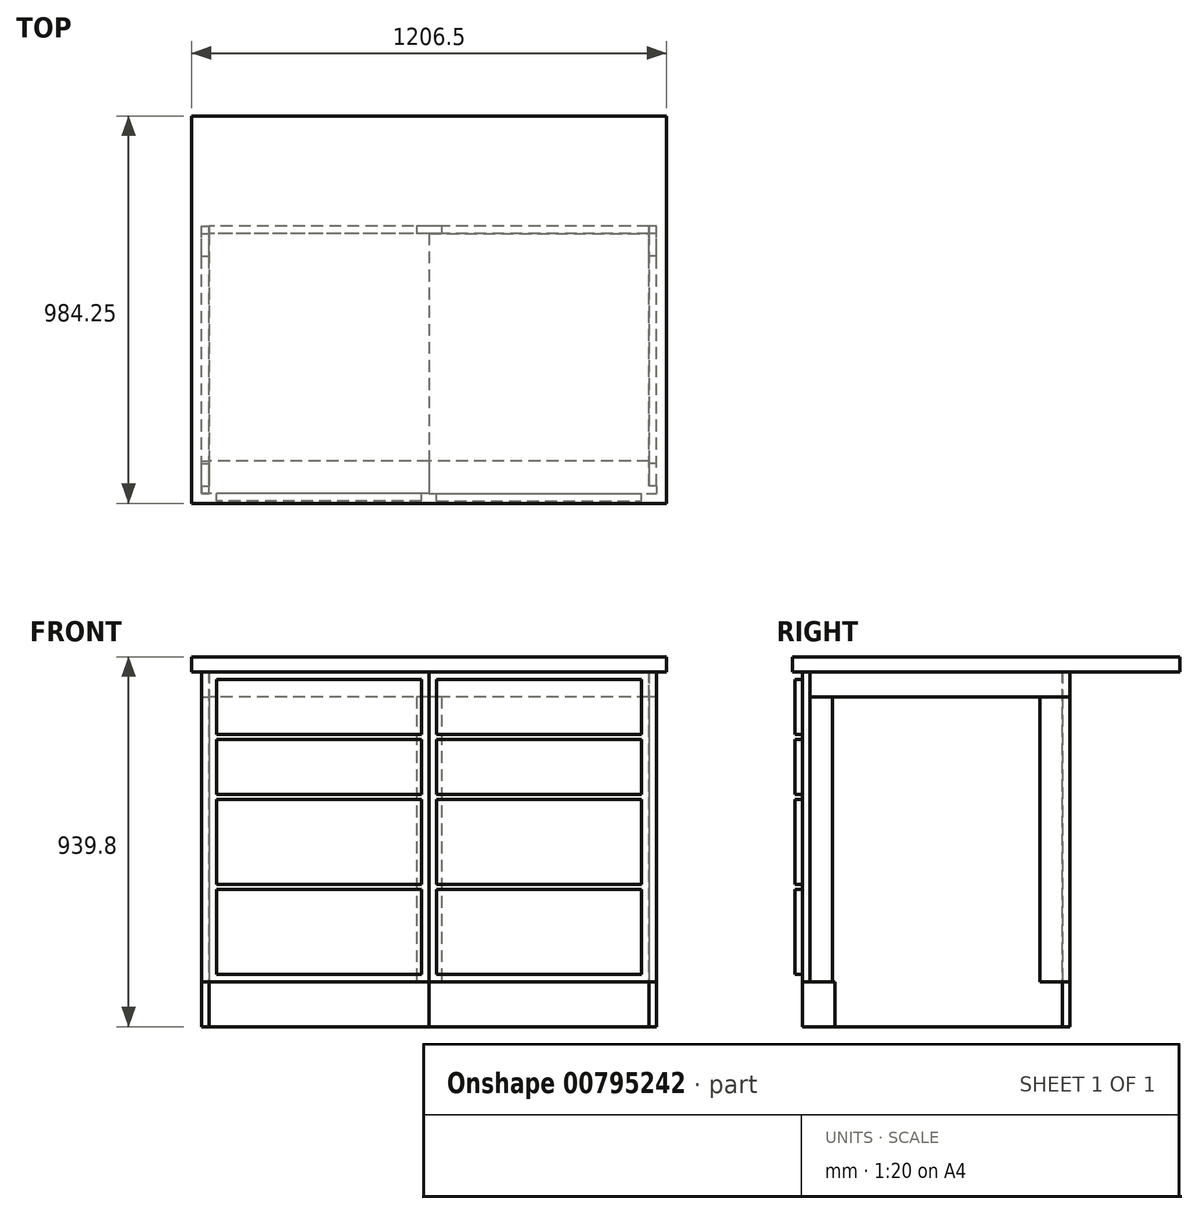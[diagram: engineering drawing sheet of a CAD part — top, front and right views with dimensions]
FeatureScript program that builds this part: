
annotation { "Feature Type Name" : "Feature", "Feature Type Description" : "" }
export const myFeature = defineFeature(function(context is Context, id is Id, definition is map)
    precondition{}
    {
        {
            var Q0;
            Q0=qCreatedBy(makeId("Top.planeOp"),FACE);
            var sketch = newSketch(context, id + "F0", { "sketchPlane" : qUnion([Q0])});
            skLineSegment(sketch, "E0.bottom", {"start": v(0, 328.85) * mm, "end": v(-558.8, 328.85) * mm});
            skLineSegment(sketch, "E0.top", {"start": v(0, -331.55) * mm, "end": v(-558.8, -331.55) * mm});
            skLineSegment(sketch, "E0.left", {"start": v(0, 328.85) * mm, "end": v(0, -331.55) * mm});
            skLineSegment(sketch, "E0.right", {"start": v(-558.8, 328.85) * mm, "end": v(-558.8, -331.55) * mm});
            skLineSegment(sketch, "E1.bottom", {"start": v(0, 328.85) * mm, "end": v(558.8, 328.85) * mm});
            skLineSegment(sketch, "E1.top", {"start": v(0, -331.55) * mm, "end": v(558.8, -331.55) * mm});
            skLineSegment(sketch, "E1.right", {"start": v(558.8, 328.85) * mm, "end": v(558.8, -331.55) * mm});
            skSolve(sketch);
        }
        {
            var Q0;
            Q0=makeQuery(id+"F0.imprint","IMPRINT",FACE,{"disambiguationData":[TD([[makeQuery(id+"F0.imprint","IMPRINT",EDGE,{"derivedFrom":sQuery(id+"F0.wireOp",EDGE,"E0.bottom")}),1.0]])]});
            extrude(context, id + "F1", {"entities" : qUnion([Q0]), "oppositeDirection" : true, "depth" : 901.7 * mm, "offsetDistance" : 25.4 * mm});
        }
        {
            var Q0;
            Q0=makeQuery(id+"F0.imprint","IMPRINT",FACE,{"disambiguationData":[TD([[makeQuery(id+"F0.imprint","IMPRINT",EDGE,{"derivedFrom":sQuery(id+"F0.wireOp",EDGE,"E1.bottom")}),-1.0]])]});
            extrude(context, id + "F2", {"entities" : qUnion([Q0]), "oppositeDirection" : true, "depth" : 901.7 * mm, "offsetDistance" : 25.4 * mm});
        }
        {
            var Q0;
            Q0=makeQuery(id+"F1.opExtrude","SWEPT_FACE",FACE,{"disambiguationData":[OSD([sQuery(id+"F0.wireOp",EDGE,"E0.top")])]});
            var sketch = newSketch(context, id + "F3", { "sketchPlane" : qUnion([Q0])});
            skLineSegment(sketch, "E2.bottom", {"start": v(-558.8, -901.7) * mm, "end": v(558.8, -901.7) * mm});
            skLineSegment(sketch, "E2.top", {"start": v(-558.8, -787.4) * mm, "end": v(558.8, -787.4) * mm});
            skLineSegment(sketch, "E2.left", {"start": v(-558.8, -901.7) * mm, "end": v(-558.8, -787.4) * mm});
            skLineSegment(sketch, "E2.right", {"start": v(558.8, -901.7) * mm, "end": v(558.8, -787.4) * mm});
            skSolve(sketch);
        }
        {
            var Q0;
            {var subQ4=sQuery(id+"F3.wireOp",EDGE,"E2.left");Q0=makeQuery(id+"F3.imprint","IMPRINT",FACE,{"disambiguationData":[TD([[makeQuery(id+"F3.imprint","IMPRINT",EDGE,{"derivedFrom":subQ4}),-1.0]])]});}
            var Q1;
            {var subQ3=sQuery(id+"F3.wireOp",EDGE,"E2.right");Q1=makeQuery(id+"F3.imprint","IMPRINT",FACE,{"disambiguationData":[TD([[makeQuery(id+"F3.imprint","IMPRINT",EDGE,{"derivedFrom":subQ3}),1.0]])]});}
            extrude(context, id + "F4", {"entities" : qUnion([Q0, Q1]), "operationType" : NewBodyOperationType.REMOVE, "oppositeDirection" : true, "depth" : 82.55 * mm, "offsetDistance" : 25.4 * mm});
        }
        {
            var Q0;
            Q0=makeQuery(id+"F1.opExtrude","SWEPT_FACE",FACE,{"disambiguationData":[OSD([sQuery(id+"F0.wireOp",EDGE,"E0.right")])]});
            var sketch = newSketch(context, id + "F5", { "sketchPlane" : qUnion([Q0])});
            skLineSegment(sketch, "E3.bottom", {"start": v(331.55, 0) * mm, "end": v(312.5, 0) * mm});
            skLineSegment(sketch, "E3.top", {"start": v(331.55, -787.4) * mm, "end": v(312.5, -787.4) * mm});
            skLineSegment(sketch, "E3.left", {"start": v(331.55, 0) * mm, "end": v(331.55, -787.4) * mm});
            skLineSegment(sketch, "E3.right", {"start": v(312.5, 0) * mm, "end": v(312.5, -787.4) * mm});
            skSolve(sketch);
        }
        {
            var Q0;
            Q0=makeQuery(id+"F5.imprint","IMPRINT",FACE,{"disambiguationData":[TD([[makeQuery(id+"F5.imprint","IMPRINT",EDGE,{"derivedFrom":sQuery(id+"F5.wireOp",EDGE,"E3.bottom")}),-1.0]])]});
            extrude(context, id + "F6", {"entities" : qUnion([Q0]), "operationType" : NewBodyOperationType.ADD, "depth" : 19.05 * mm, "offsetDistance" : 25.4 * mm});
        }
        {
            var Q0;
            Q0=makeQuery(id+"F2.opExtrude","SWEPT_FACE",FACE,{"disambiguationData":[OSD([sQuery(id+"F0.wireOp",EDGE,"E1.right")])]});
            var sketch = newSketch(context, id + "F7", { "sketchPlane" : qUnion([Q0])});
            skLineSegment(sketch, "E4.bottom", {"start": v(-331.55, 0) * mm, "end": v(-312.5, 0) * mm});
            skLineSegment(sketch, "E4.top", {"start": v(-331.55, -787.4) * mm, "end": v(-312.5, -787.4) * mm});
            skLineSegment(sketch, "E4.left", {"start": v(-331.55, 0) * mm, "end": v(-331.55, -787.4) * mm});
            skLineSegment(sketch, "E4.right", {"start": v(-312.5, 0) * mm, "end": v(-312.5, -787.4) * mm});
            skSolve(sketch);
        }
        {
            var Q0;
            Q0=makeQuery(id+"F7.imprint","IMPRINT",FACE,{"disambiguationData":[TD([[makeQuery(id+"F7.imprint","IMPRINT",EDGE,{"derivedFrom":sQuery(id+"F7.wireOp",EDGE,"E4.bottom")}),1.0]])]});
            extrude(context, id + "F8", {"entities" : qUnion([Q0]), "operationType" : NewBodyOperationType.ADD, "depth" : 19.05 * mm, "offsetDistance" : 25.4 * mm});
        }
        {
            var Q0;
            Q0=makeQuery(id+"F1.opExtrude","SWEPT_FACE",FACE,{"disambiguationData":[OSD([sQuery(id+"F0.wireOp",EDGE,"E0.right")])]});
            var sketch = newSketch(context, id + "F9", { "sketchPlane" : qUnion([Q0])});
            skLineSegment(sketch, "E5.bottom", {"start": v(331.55, -901.7) * mm, "end": v(-347.9, -901.7) * mm});
            skLineSegment(sketch, "E5.top", {"start": v(331.55, -787.4) * mm, "end": v(-347.9, -787.4) * mm});
            skLineSegment(sketch, "E5.left", {"start": v(331.55, -901.7) * mm, "end": v(331.55, -787.4) * mm});
            skLineSegment(sketch, "E5.right", {"start": v(-347.9, -901.7) * mm, "end": v(-347.9, -787.4) * mm});
            skLineSegment(sketch, "E6.bottom", {"start": v(331.55, 0) * mm, "end": v(-347.9, 0) * mm});
            skLineSegment(sketch, "E6.top", {"start": v(331.55, -63.5) * mm, "end": v(-347.9, -63.5) * mm});
            skLineSegment(sketch, "E6.left", {"start": v(331.55, 0) * mm, "end": v(331.55, -63.5) * mm});
            skLineSegment(sketch, "E6.right", {"start": v(-347.9, 0) * mm, "end": v(-347.9, -63.5) * mm});
            skLineSegment(sketch, "E7.bottom", {"start": v(-347.9, -63.5) * mm, "end": v(-271.7, -63.5) * mm});
            skLineSegment(sketch, "E7.top", {"start": v(-347.9, -787.4) * mm, "end": v(-271.7, -787.4) * mm});
            skLineSegment(sketch, "E7.left", {"start": v(-347.9, -63.5) * mm, "end": v(-347.9, -787.4) * mm});
            skLineSegment(sketch, "E7.right", {"start": v(-271.7, -63.5) * mm, "end": v(-271.7, -787.4) * mm});
            skLineSegment(sketch, "E8.bottom", {"start": v(331.55, -63.5) * mm, "end": v(255.35, -63.5) * mm});
            skLineSegment(sketch, "E8.top", {"start": v(331.55, -787.4) * mm, "end": v(255.35, -787.4) * mm});
            skLineSegment(sketch, "E8.left", {"start": v(331.55, -63.5) * mm, "end": v(331.55, -787.4) * mm});
            skLineSegment(sketch, "E8.right", {"start": v(255.35, -63.5) * mm, "end": v(255.35, -787.4) * mm});
            skSolve(sketch);
        }
        {
            var Q0;
            {var subQ0=makeQuery(id+"F4.boolean.opBoolean","COPY",EDGE,{"derivedFrom":makeQuery(id+"F4.opExtrude","CAP_EDGE",EDGE,{"disambiguationData":[OSD([sQuery(id+"F3.wireOp",EDGE,"E2.left")])],"isStart":false})});Q0=makeQuery(id+"F9.imprint","IMPRINT",FACE,{"disambiguationData":[TD([[makeQuery(id+"F9.imprint","IMPRINT",EDGE,{"derivedFrom":subQ0}),1.0]])]});}
            var Q1;
            {var subQ3=sQuery(id+"F9.wireOp",EDGE,"E6.right");Q1=makeQuery(id+"F9.imprint","IMPRINT",FACE,{"disambiguationData":[TD([[makeQuery(id+"F9.imprint","IMPRINT",EDGE,{"derivedFrom":subQ3}),1.0]])]});}
            var Q2;
            {var subQ1=sQuery(id+"F9.wireOp",EDGE,"E6.top");Q2=makeQuery(id+"F9.imprint","IMPRINT",FACE,{"disambiguationData":[TD([[makeQuery(id+"F9.imprint","IMPRINT",EDGE,{"derivedFrom":subQ1}),-1.0]])]});}
            var Q3;
            {var subQ3=sQuery(id+"F9.wireOp",EDGE,"E5.right");Q3=makeQuery(id+"F9.imprint","IMPRINT",FACE,{"disambiguationData":[TD([[makeQuery(id+"F9.imprint","IMPRINT",EDGE,{"derivedFrom":subQ3}),-1.0]])]});}
            var Q4;
            {var subQ2=sQuery(id+"F9.wireOp",EDGE,"E5.left");Q4=makeQuery(id+"F9.imprint","IMPRINT",FACE,{"disambiguationData":[TD([[makeQuery(id+"F9.imprint","IMPRINT",EDGE,{"derivedFrom":subQ2}),1.0]])]});}
            extrude(context, id + "F10", {"entities" : qUnion([Q0, Q1, Q2, Q3, Q4]), "depth" : 19.05 * mm, "offsetDistance" : 25.4 * mm});
        }
        {
            var Q0;
            {var subQ0=sQuery(id+"F9.wireOp",EDGE,"E7.right");Q0=makeQuery(id+"F9.imprint","IMPRINT",FACE,{"disambiguationData":[TD([[makeQuery(id+"F9.imprint","IMPRINT",EDGE,{"derivedFrom":subQ0}),-1.0]])]});}
            var Q1;
            {var subQ0=sQuery(id+"F9.wireOp",EDGE,"E7.left");Q1=makeQuery(id+"F9.imprint","IMPRINT",FACE,{"disambiguationData":[TD([[makeQuery(id+"F9.imprint","IMPRINT",EDGE,{"derivedFrom":subQ0}),1.0]])]});}
            var Q2;
            {var subQ0=sQuery(id+"F9.wireOp",EDGE,"E8.right");Q2=makeQuery(id+"F9.imprint","IMPRINT",FACE,{"disambiguationData":[TD([[makeQuery(id+"F9.imprint","IMPRINT",EDGE,{"derivedFrom":subQ0}),1.0]])]});}
            extrude(context, id + "F11", {"entities" : qUnion([Q0, Q1, Q2]), "depth" : 19.05 * mm, "offsetDistance" : 25.4 * mm});
        }
        {
            var Q0;
            Q0=makeQuery(id+"F10.opExtrude","SWEPT_BODY",BODY,{"disambiguationData":[OSD([sQuery(id+"F5.wireOp",EDGE,"E3.right"),sQuery(id+"F9.wireOp",EDGE,"E6.bottom"),sQuery(id+"F9.wireOp",EDGE,"E6.top"),sQuery(id+"F9.wireOp",EDGE,"E6.right"),sQuery(id+"F9.wireOp",EDGE,"E7.bottom"),sQuery(id+"F9.wireOp",EDGE,"E8.bottom")])]});
            var Q1;
            Q1=makeQuery(id+"F11.opExtrude","SWEPT_BODY",BODY,{"disambiguationData":[OSD([sQuery(id+"F9.wireOp",EDGE,"E7.bottom"),sQuery(id+"F9.wireOp",EDGE,"E7.top"),sQuery(id+"F9.wireOp",EDGE,"E7.left"),sQuery(id+"F9.wireOp",EDGE,"E7.right")])]});
            var Q2;
            Q2=makeQuery(id+"F10.opExtrude","SWEPT_BODY",BODY,{"disambiguationData":[OSD([sQuery(id+"F9.wireOp",EDGE,"E5.bottom"),sQuery(id+"F9.wireOp",EDGE,"E5.top"),sQuery(id+"F9.wireOp",EDGE,"E5.left"),sQuery(id+"F9.wireOp",EDGE,"E5.right"),sQuery(id+"F9.wireOp",EDGE,"E7.top"),sQuery(id+"F9.wireOp",EDGE,"E8.top")])]});
            var Q3;
            Q3=makeQuery(id+"F11.opExtrude","SWEPT_BODY",BODY,{"disambiguationData":[OSD([sQuery(id+"F5.wireOp",EDGE,"E3.right"),sQuery(id+"F9.wireOp",EDGE,"E8.bottom"),sQuery(id+"F9.wireOp",EDGE,"E8.top"),sQuery(id+"F9.wireOp",EDGE,"E8.right")])]});
            var Q4;
            Q4=qCreatedBy(makeId("Right.planeOp"),FACE);
            mirror(context, id + "F12", {"entities" : qUnion([Q0, Q1, Q2, Q3]), "mirrorPlane" : qUnion([Q4])});
        }
        {
            var Q0;
            Q0=makeQuery(id+"F2.opExtrude","SWEPT_FACE",FACE,{"disambiguationData":[OSD([sQuery(id+"F0.wireOp",EDGE,"E1.bottom")])]});
            var sketch = newSketch(context, id + "F13", { "sketchPlane" : qUnion([Q0])});
            skLineSegment(sketch, "E9.bottom", {"start": v(-558.8, 0) * mm, "end": v(558.8, 0) * mm});
            skLineSegment(sketch, "E9.top", {"start": v(-558.8, -63.5) * mm, "end": v(558.8, -63.5) * mm});
            skLineSegment(sketch, "E9.left", {"start": v(-558.8, 0) * mm, "end": v(-558.8, -63.5) * mm});
            skLineSegment(sketch, "E9.right", {"start": v(558.8, 0) * mm, "end": v(558.8, -63.5) * mm});
            skLineSegment(sketch, "E10.bottom", {"start": v(-558.8, -787.4) * mm, "end": v(558.8, -787.4) * mm});
            skLineSegment(sketch, "E10.top", {"start": v(-558.8, -901.7) * mm, "end": v(558.8, -901.7) * mm});
            skLineSegment(sketch, "E10.left", {"start": v(-558.8, -787.4) * mm, "end": v(-558.8, -901.7) * mm});
            skLineSegment(sketch, "E10.right", {"start": v(558.8, -787.4) * mm, "end": v(558.8, -901.7) * mm});
            skLineSegment(sketch, "E11.bottom", {"start": v(-558.8, -63.5) * mm, "end": v(-514.35, -63.5) * mm});
            skLineSegment(sketch, "E11.top", {"start": v(-558.8, -787.4) * mm, "end": v(-514.35, -787.4) * mm});
            skLineSegment(sketch, "E11.left", {"start": v(-558.8, -63.5) * mm, "end": v(-558.8, -787.4) * mm});
            skLineSegment(sketch, "E11.right", {"start": v(-514.35, -63.5) * mm, "end": v(-514.35, -787.4) * mm});
            skLineSegment(sketch, "E12.bottom", {"start": v(558.8, -63.5) * mm, "end": v(514.35, -63.5) * mm});
            skLineSegment(sketch, "E12.top", {"start": v(558.8, -787.4) * mm, "end": v(514.35, -787.4) * mm});
            skLineSegment(sketch, "E12.left", {"start": v(558.8, -63.5) * mm, "end": v(558.8, -787.4) * mm});
            skLineSegment(sketch, "E12.right", {"start": v(514.35, -63.5) * mm, "end": v(514.35, -787.4) * mm});
            skLineSegment(sketch, "E13.bottom", {"start": v(-31.75, -63.5) * mm, "end": v(31.75, -63.5) * mm});
            skLineSegment(sketch, "E13.top", {"start": v(-31.75, -787.4) * mm, "end": v(31.75, -787.4) * mm});
            skLineSegment(sketch, "E13.left", {"start": v(-31.75, -63.5) * mm, "end": v(-31.75, -787.4) * mm});
            skLineSegment(sketch, "E13.right", {"start": v(31.75, -63.5) * mm, "end": v(31.75, -787.4) * mm});
            skPoint(sketch, "E14", {"position": v(0, -63.5) * mm});
            skSolve(sketch);
        }
        {
            var Q0;
            {var subQ0=sQuery(id+"F13.wireOp",EDGE,"E9.left");Q0=makeQuery(id+"F13.imprint","IMPRINT",FACE,{"disambiguationData":[TD([[makeQuery(id+"F13.imprint","IMPRINT",EDGE,{"derivedFrom":subQ0}),-1.0]])]});}
            var Q1;
            {var subQ0=sQuery(id+"F13.wireOp",EDGE,"E9.right");Q1=makeQuery(id+"F13.imprint","IMPRINT",FACE,{"disambiguationData":[TD([[makeQuery(id+"F13.imprint","IMPRINT",EDGE,{"derivedFrom":subQ0}),-1.0]])]});}
            var Q2;
            {var subQ0=sQuery(id+"F13.wireOp",EDGE,"E10.left");Q2=makeQuery(id+"F13.imprint","IMPRINT",FACE,{"disambiguationData":[TD([[makeQuery(id+"F13.imprint","IMPRINT",EDGE,{"derivedFrom":subQ0}),-1.0]])]});}
            var Q3;
            {var subQ0=sQuery(id+"F13.wireOp",EDGE,"E10.right");Q3=makeQuery(id+"F13.imprint","IMPRINT",FACE,{"disambiguationData":[TD([[makeQuery(id+"F13.imprint","IMPRINT",EDGE,{"derivedFrom":subQ0}),-1.0]])]});}
            extrude(context, id + "F14", {"entities" : qUnion([Q0, Q1, Q2, Q3]), "depth" : 19.05 * mm, "offsetDistance" : 25.4 * mm});
        }
        {
            var Q0;
            Q0=makeQuery(id+"F13.imprint","IMPRINT",FACE,{"disambiguationData":[TD([[makeQuery(id+"F13.imprint","IMPRINT",EDGE,{"derivedFrom":sQuery(id+"F13.wireOp",EDGE,"E11.bottom")}),-1.0]])]});
            var Q1;
            {var subQ0=sQuery(id+"F13.wireOp",EDGE,"E13.right");Q1=makeQuery(id+"F13.imprint","IMPRINT",FACE,{"disambiguationData":[TD([[makeQuery(id+"F13.imprint","IMPRINT",EDGE,{"derivedFrom":subQ0}),-1.0]])]});}
            var Q2;
            {var subQ0=sQuery(id+"F13.wireOp",EDGE,"E13.left");Q2=makeQuery(id+"F13.imprint","IMPRINT",FACE,{"disambiguationData":[TD([[makeQuery(id+"F13.imprint","IMPRINT",EDGE,{"derivedFrom":subQ0}),1.0]])]});}
            var Q3;
            Q3=makeQuery(id+"F13.imprint","IMPRINT",FACE,{"disambiguationData":[TD([[makeQuery(id+"F13.imprint","IMPRINT",EDGE,{"derivedFrom":sQuery(id+"F13.wireOp",EDGE,"E12.bottom")}),1.0]])]});
            extrude(context, id + "F15", {"entities" : qUnion([Q0, Q1, Q2, Q3]), "depth" : 19.05 * mm, "offsetDistance" : 25.4 * mm});
        }
        {
            var Q0;
            Q0=makeQuery(id+"F0.imprint","IMPRINT",FACE,{"disambiguationData":[TD([[makeQuery(id+"F0.imprint","IMPRINT",EDGE,{"derivedFrom":sQuery(id+"F0.wireOp",EDGE,"E0.bottom")}),1.0]])]});
            var sketch = newSketch(context, id + "F16", { "sketchPlane" : qUnion([Q0])});
            skLineSegment(sketch, "E15.bottom", {"start": v(-603.25, -356.95) * mm, "end": v(603.25, -356.95) * mm});
            skLineSegment(sketch, "E15.top", {"start": v(-603.25, 627.3) * mm, "end": v(603.25, 627.3) * mm});
            skLineSegment(sketch, "E15.left", {"start": v(-603.25, -356.95) * mm, "end": v(-603.25, 627.3) * mm});
            skLineSegment(sketch, "E15.right", {"start": v(603.25, -356.95) * mm, "end": v(603.25, 627.3) * mm});
            skSolve(sketch);
        }
        {
            var Q0;
            Q0=makeQuery(id+"F16.imprint","IMPRINT",FACE,{"disambiguationData":[TD([[makeQuery(id+"F16.imprint","IMPRINT",EDGE,{"derivedFrom":sQuery(id+"F16.wireOp",EDGE,"E15.bottom")}),1.0]])]});
            var Q1;
            Q1=makeQuery(id+"F16.imprint","IMPRINT",FACE,{"disambiguationData":[TD([[makeQuery(id+"F16.imprint","IMPRINT",EDGE,{"derivedFrom":makeQuery(id+"F0.imprint","IMPRINT",EDGE,{"derivedFrom":sQuery(id+"F0.wireOp",EDGE,"E0.bottom")})}),1.0]])]});
            extrude(context, id + "F17", {"entities" : qUnion([Q0, Q1]), "depth" : 38.1 * mm, "offsetDistance" : 25.4 * mm});
        }
        {
            var Q0;
            Q0=makeQuery(id+"F6.boolean.opBoolean","MERGE",FACE,{"derivedFrom":[makeQuery(id+"F1.opExtrude","SWEPT_FACE",FACE,{"disambiguationData":[OSD([sQuery(id+"F0.wireOp",EDGE,"E0.top")])]}),makeQuery(id+"F6.opExtrude","SWEPT_FACE",FACE,{"disambiguationData":[OSD([sQuery(id+"F5.wireOp",EDGE,"E3.left")])]})]});
            var sketch = newSketch(context, id + "F18", { "sketchPlane" : qUnion([Q0])});
            skLineSegment(sketch, "E16.bottom", {"start": v(-19.05, -19.05) * mm, "end": v(-539.75, -19.05) * mm});
            skLineSegment(sketch, "E16.top", {"start": v(-19.05, -158.75) * mm, "end": v(-539.75, -158.75) * mm});
            skLineSegment(sketch, "E16.left", {"start": v(-19.05, -19.05) * mm, "end": v(-19.05, -158.75) * mm});
            skLineSegment(sketch, "E16.right", {"start": v(-539.75, -19.05) * mm, "end": v(-539.75, -158.75) * mm});
            skLineSegment(sketch, "E17.bottom", {"start": v(-539.75, -171.45) * mm, "end": v(-19.05, -171.45) * mm});
            skLineSegment(sketch, "E17.top", {"start": v(-539.75, -311.15) * mm, "end": v(-19.05, -311.15) * mm});
            skLineSegment(sketch, "E17.left", {"start": v(-539.75, -171.45) * mm, "end": v(-539.75, -311.15) * mm});
            skLineSegment(sketch, "E17.right", {"start": v(-19.05, -171.45) * mm, "end": v(-19.05, -311.15) * mm});
            skLineSegment(sketch, "E18.bottom", {"start": v(-19.05, -323.85) * mm, "end": v(-539.75, -323.85) * mm});
            skLineSegment(sketch, "E18.top", {"start": v(-19.05, -539.75) * mm, "end": v(-539.75, -539.75) * mm});
            skLineSegment(sketch, "E18.left", {"start": v(-19.05, -323.85) * mm, "end": v(-19.05, -539.75) * mm});
            skLineSegment(sketch, "E18.right", {"start": v(-539.75, -323.85) * mm, "end": v(-539.75, -539.75) * mm});
            skLineSegment(sketch, "E19.bottom", {"start": v(-539.75, -552.45) * mm, "end": v(-19.05, -552.45) * mm});
            skLineSegment(sketch, "E19.top", {"start": v(-539.75, -768.35) * mm, "end": v(-19.05, -768.35) * mm});
            skLineSegment(sketch, "E19.left", {"start": v(-539.75, -552.45) * mm, "end": v(-539.75, -768.35) * mm});
            skLineSegment(sketch, "E19.right", {"start": v(-19.05, -552.45) * mm, "end": v(-19.05, -768.35) * mm});
            skLineSegment(sketch, "E20.MirrorCS", {"start": v(539.75, -311.15) * mm, "end": v(19.05, -311.15) * mm});
            skLineSegment(sketch, "E21.MirrorCS", {"start": v(539.75, -171.45) * mm, "end": v(19.05, -171.45) * mm});
            skLineSegment(sketch, "E22.MirrorCS", {"start": v(19.05, -539.75) * mm, "end": v(539.75, -539.75) * mm});
            skLineSegment(sketch, "E23.MirrorCS", {"start": v(539.75, -19.05) * mm, "end": v(539.75, -158.75) * mm});
            skLineSegment(sketch, "E24.MirrorCS", {"start": v(19.05, -323.85) * mm, "end": v(539.75, -323.85) * mm});
            skLineSegment(sketch, "E25.MirrorCS", {"start": v(19.05, -19.05) * mm, "end": v(19.05, -158.75) * mm});
            skLineSegment(sketch, "E26.MirrorCS", {"start": v(19.05, -552.45) * mm, "end": v(19.05, -768.35) * mm});
            skLineSegment(sketch, "E27.MirrorCS", {"start": v(539.75, -171.45) * mm, "end": v(539.75, -311.15) * mm});
            skLineSegment(sketch, "E28.MirrorCS", {"start": v(19.05, -19.05) * mm, "end": v(539.75, -19.05) * mm});
            skLineSegment(sketch, "E29.MirrorCS", {"start": v(539.75, -552.45) * mm, "end": v(539.75, -768.35) * mm});
            skLineSegment(sketch, "E30.MirrorCS", {"start": v(539.75, -768.35) * mm, "end": v(19.05, -768.35) * mm});
            skLineSegment(sketch, "E31.MirrorCS", {"start": v(539.75, -323.85) * mm, "end": v(539.75, -539.75) * mm});
            skLineSegment(sketch, "E32.MirrorCS", {"start": v(19.05, -158.75) * mm, "end": v(539.75, -158.75) * mm});
            skLineSegment(sketch, "E33.MirrorCS", {"start": v(19.05, -323.85) * mm, "end": v(19.05, -539.75) * mm});
            skLineSegment(sketch, "E34.MirrorCS", {"start": v(539.75, -552.45) * mm, "end": v(19.05, -552.45) * mm});
            skLineSegment(sketch, "E35.MirrorCS", {"start": v(19.05, -171.45) * mm, "end": v(19.05, -311.15) * mm});
            skSolve(sketch);
        }
        {
            var Q0;
            Q0=makeQuery(id+"F18.imprint","IMPRINT",FACE,{"disambiguationData":[TD([[makeQuery(id+"F18.imprint","IMPRINT",EDGE,{"derivedFrom":sQuery(id+"F18.wireOp",EDGE,"E16.bottom")}),1.0]])]});
            var Q1;
            Q1=makeQuery(id+"F18.imprint","IMPRINT",FACE,{"disambiguationData":[TD([[makeQuery(id+"F18.imprint","IMPRINT",EDGE,{"derivedFrom":sQuery(id+"F18.wireOp",EDGE,"E23.MirrorCS")}),-1.0]])]});
            var Q2;
            Q2=makeQuery(id+"F18.imprint","IMPRINT",FACE,{"disambiguationData":[TD([[makeQuery(id+"F18.imprint","IMPRINT",EDGE,{"derivedFrom":sQuery(id+"F18.wireOp",EDGE,"E20.MirrorCS")}),-1.0]])]});
            var Q3;
            Q3=makeQuery(id+"F18.imprint","IMPRINT",FACE,{"disambiguationData":[TD([[makeQuery(id+"F18.imprint","IMPRINT",EDGE,{"derivedFrom":sQuery(id+"F18.wireOp",EDGE,"E17.bottom")}),-1.0]])]});
            var Q4;
            Q4=makeQuery(id+"F18.imprint","IMPRINT",FACE,{"disambiguationData":[TD([[makeQuery(id+"F18.imprint","IMPRINT",EDGE,{"derivedFrom":sQuery(id+"F18.wireOp",EDGE,"E18.bottom")}),1.0]])]});
            var Q5;
            Q5=makeQuery(id+"F18.imprint","IMPRINT",FACE,{"disambiguationData":[TD([[makeQuery(id+"F18.imprint","IMPRINT",EDGE,{"derivedFrom":sQuery(id+"F18.wireOp",EDGE,"E22.MirrorCS")}),1.0]])]});
            var Q6;
            Q6=makeQuery(id+"F18.imprint","IMPRINT",FACE,{"disambiguationData":[TD([[makeQuery(id+"F18.imprint","IMPRINT",EDGE,{"derivedFrom":sQuery(id+"F18.wireOp",EDGE,"E26.MirrorCS")}),1.0]])]});
            var Q7;
            Q7=makeQuery(id+"F18.imprint","IMPRINT",FACE,{"disambiguationData":[TD([[makeQuery(id+"F18.imprint","IMPRINT",EDGE,{"derivedFrom":sQuery(id+"F18.wireOp",EDGE,"E19.bottom")}),-1.0]])]});
            extrude(context, id + "F19", {"entities" : qUnion([Q0, Q1, Q2, Q3, Q4, Q5, Q6, Q7]), "depth" : 19.05 * mm, "offsetDistance" : 25.4 * mm});
        }
    });
